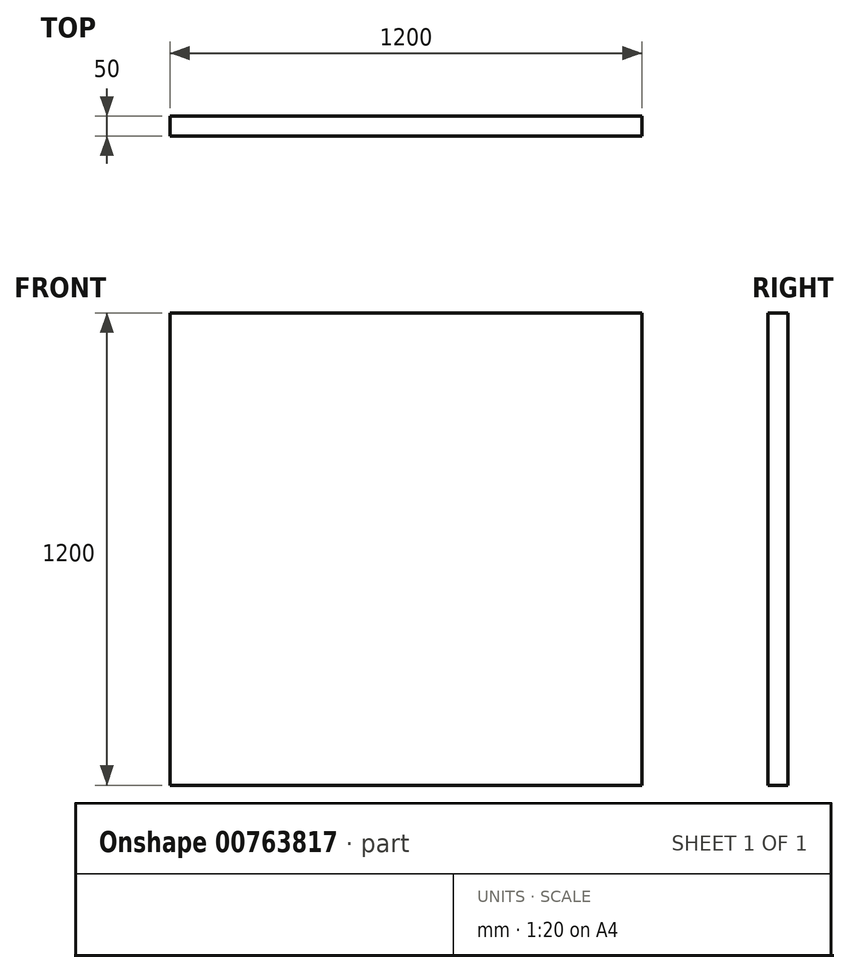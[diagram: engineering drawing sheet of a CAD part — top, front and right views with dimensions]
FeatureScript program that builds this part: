
annotation { "Feature Type Name" : "Feature", "Feature Type Description" : "" }
export const myFeature = defineFeature(function(context is Context, id is Id, definition is map)
    precondition{}
    {
        {
            var Q0;
            Q0=qCreatedBy(makeId("Front.planeOp"),FACE);
            var sketch = newSketch(context, id + "F0", { "sketchPlane" : qUnion([Q0])});
            skLineSegment(sketch, "E0", {"start": v(-78.83, 548.92) * mm, "end": v(-78.83, -651.08) * mm});
            skLineSegment(sketch, "E1", {"start": v(-78.83, -651.08) * mm, "end": v(1121.17, -651.08) * mm});
            skLineSegment(sketch, "E2", {"start": v(-78.83, 548.92) * mm, "end": v(1121.17, 548.92) * mm});
            skLineSegment(sketch, "E3", {"start": v(1121.17, 548.92) * mm, "end": v(1121.17, -651.08) * mm});
            skSolve(sketch);
        }
        {
            var Q0;
            Q0 = qSketchRegion(id + "F0", true);
            extrude(context, id + "F1", {"entities" : qUnion([Q0]), "depth" : 50 * mm, "offsetDistance" : 25 * mm});
        }
    });
